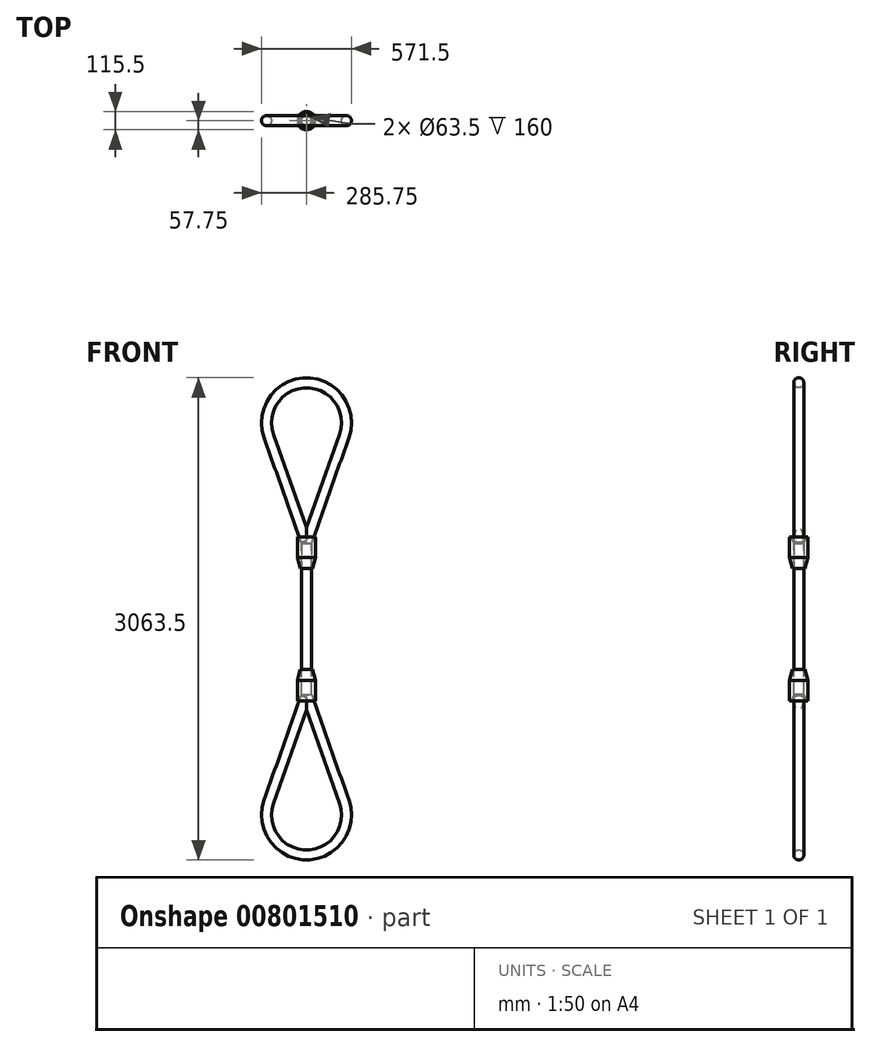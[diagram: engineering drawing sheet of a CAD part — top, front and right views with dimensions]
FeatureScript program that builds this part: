
annotation { "Feature Type Name" : "Feature", "Feature Type Description" : "" }
export const myFeature = defineFeature(function(context is Context, id is Id, definition is map)
    precondition{}
    {
        {
            var Q0;
            Q0=qCreatedBy(makeId("Top.planeOp"),FACE);
            var sketch = newSketch(context, id + "F0", { "sketchPlane" : qUnion([Q0])});
            skCircle(sketch, "E0", {"center": v(0, 0) * mm, "radius": 31.75 * mm});
            skSolve(sketch);
        }
        {
            var Q0;
            Q0=qCreatedBy(makeId("Front.planeOp"),FACE);
            var sketch = newSketch(context, id + "F1", { "sketchPlane" : qUnion([Q0])});
            skLineSegment(sketch, "E1", {"start": v(0, 0) * mm, "end": v(0, 484) * mm});
            skLineSegment(sketch, "E2", {"start": v(0, 484) * mm, "end": v(0, 1500) * mm, "construction": true});
            skLineSegment(sketch, "E3", {"start": v(0, 484) * mm, "end": v(239.47, 1161.33) * mm});
            skArc(sketch, "E4", {"start": v(239.47, 1161.33) * mm, "mid": v(207.4, 1392.65) * mm, "end": v(0, 1500) * mm});
            skArc(sketch, "E5.MirrorCS", {"start": v(-239.47, 1161.33) * mm, "mid": v(-207.4, 1392.65) * mm, "end": v(0, 1500) * mm});
            skLineSegment(sketch, "E6", {"start": v(-239.47, 1161.33) * mm, "end": v(-4.51, 496.76) * mm});
            skSolve(sketch);
        }
        {
            var Q0;
            Q0=makeQuery(id+"F0.imprint","IMPRINT",FACE,{"disambiguationData":[TD([[makeQuery(id+"F0.imprint","IMPRINT",EDGE,{"derivedFrom":sQuery(id+"F0.wireOp",EDGE,"E0")}),1.0]])]});
            var Q1;
            Q1=sQuery(id+"F1.wireOp",EDGE,"E1");
            var Q2;
            Q2=sQuery(id+"F1.wireOp",EDGE,"E3");
            var Q3;
            Q3=sQuery(id+"F1.wireOp",EDGE,"E4");
            var Q4;
            Q4=sQuery(id+"F1.wireOp",EDGE,"E5.MirrorCS");
            var Q5;
            Q5=sQuery(id+"F1.wireOp",EDGE,"E6");
            sweep(context, id + "F2", {"profiles" : qUnion([Q0]), "path" : qUnion([Q1, Q2, Q3, Q4, Q5])});
        }
        {
            var Q0;
            Q0=makeQuery(id+"F2.opSweep","SWEPT_BODY",BODY,{"disambiguationData":[OSD([sQuery(id+"F0.wireOp",EDGE,"E0"),sQuery(id+"F1.wireOp",EDGE,"E6")])]});
            var Q1;
            Q1=qCreatedBy(makeId("Top.planeOp"),FACE);
            mirror(context, id + "F3", {"operationType" : NewBodyOperationType.ADD, "entities" : qUnion([Q0]), "mirrorPlane" : qUnion([Q1])});
        }
        {
            var Q0;
            Q0=qCreatedBy(makeId("Front.planeOp"),FACE);
            var sketch = newSketch(context, id + "F4", { "sketchPlane" : qUnion([Q0])});
            skLineSegment(sketch, "E7", {"start": v(31.75, 320) * mm, "end": v(31.75, 480) * mm});
            skLineSegment(sketch, "E8", {"start": v(31.75, 480) * mm, "end": v(47.75, 520) * mm});
            skLineSegment(sketch, "E9", {"start": v(47.75, 520) * mm, "end": v(57.75, 520) * mm});
            skLineSegment(sketch, "E10", {"start": v(57.75, 520) * mm, "end": v(57.75, 390) * mm});
            skLineSegment(sketch, "E11", {"start": v(57.75, 390) * mm, "end": v(39.75, 320) * mm});
            skLineSegment(sketch, "E12", {"start": v(39.75, 320) * mm, "end": v(31.75, 320) * mm});
            skSolve(sketch);
        }
        {
            var Q0;
            Q0=qCreatedBy(makeId("Front.planeOp"),FACE);
            var sketch = newSketch(context, id + "F5", { "sketchPlane" : qUnion([Q0])});
            skLineSegment(sketch, "E13", {"start": v(0, 0) * mm, "end": v(0, 542.03) * mm});
            skSolve(sketch);
        }
        {
            var Q0;
            Q0=makeQuery(id+"F4.imprint","IMPRINT",FACE,{"disambiguationData":[TD([[makeQuery(id+"F4.imprint","IMPRINT",EDGE,{"derivedFrom":sQuery(id+"F4.wireOp",EDGE,"E7")}),-1.0]])]});
            var Q1;
            Q1=sQuery(id+"F5.wireOp",EDGE,"E13");
            revolve(context, id + "F6", {"surfaceOperationType" : NewSurfaceOperationType.NEW, "entities" : qUnion([Q0]), "axis" : qUnion([Q1]), "revolveType" : RevolveType.FULL});
        }
        {
            var Q0;
            Q0=makeQuery(id+"F6.opRevolve","SWEPT_BODY",BODY,{"disambiguationData":[OSD([sQuery(id+"F4.wireOp",EDGE,"E7"),sQuery(id+"F4.wireOp",EDGE,"E8"),sQuery(id+"F4.wireOp",EDGE,"E9"),sQuery(id+"F4.wireOp",EDGE,"E10"),sQuery(id+"F4.wireOp",EDGE,"E11"),sQuery(id+"F4.wireOp",EDGE,"E12")])]});
            var Q1;
            Q1=qCreatedBy(makeId("Top.planeOp"),FACE);
            mirror(context, id + "F7", {"entities" : qUnion([Q0]), "mirrorPlane" : qUnion([Q1])});
        }
    });
